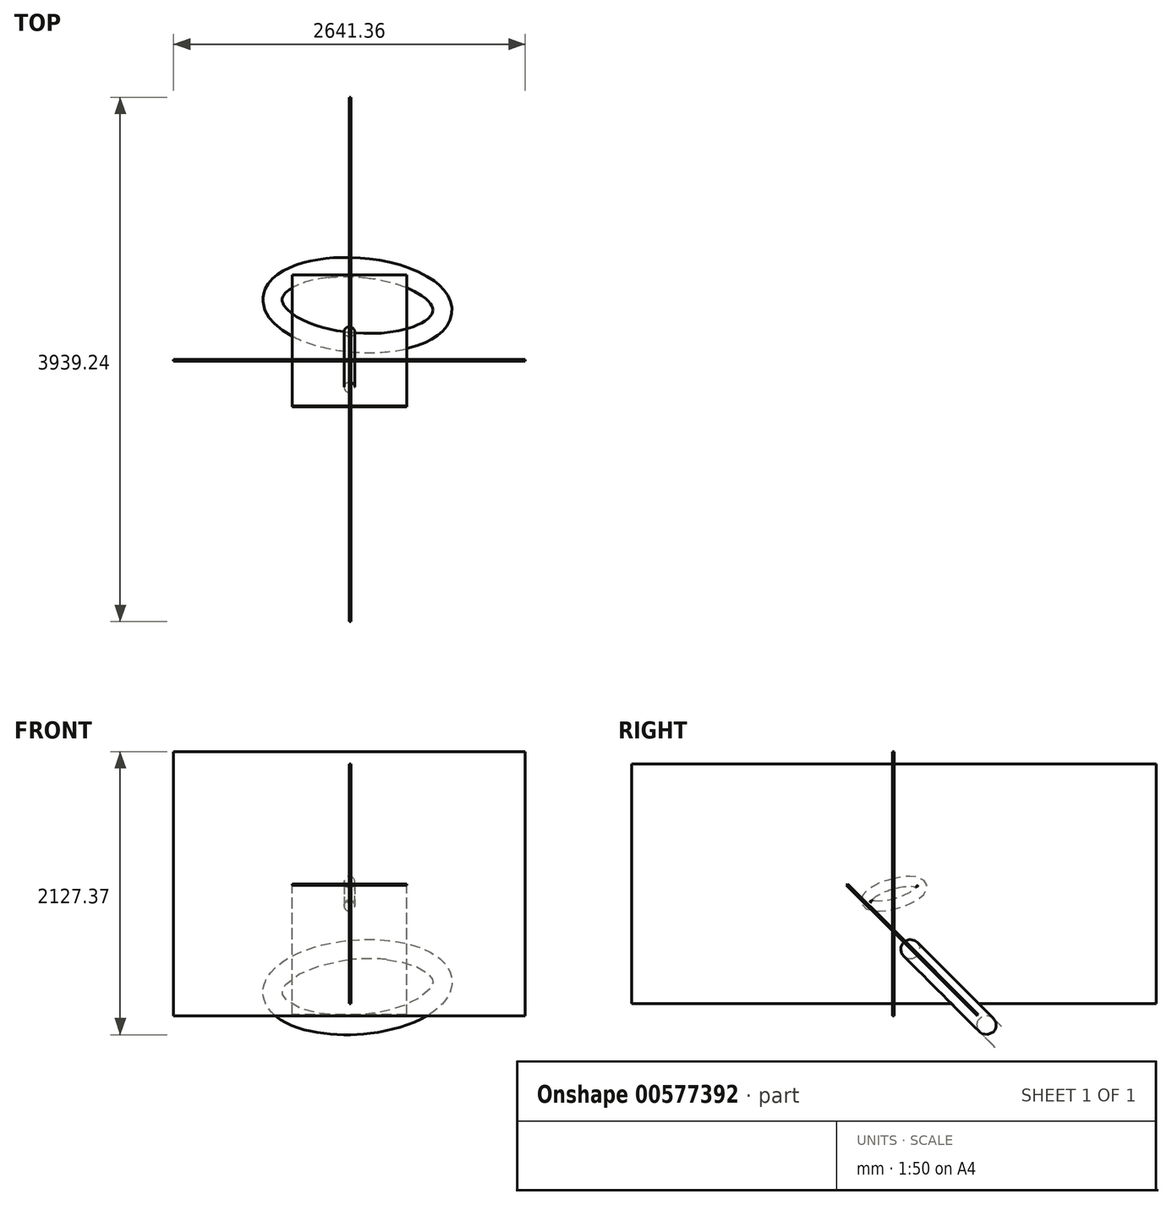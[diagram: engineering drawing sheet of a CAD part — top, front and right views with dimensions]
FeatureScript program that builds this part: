
annotation { "Feature Type Name" : "Feature", "Feature Type Description" : "" }
export const myFeature = defineFeature(function(context is Context, id is Id, definition is map)
    precondition{}
    {
        {
            var Q0;
            Q0=qCreatedBy(makeId("Front.planeOp"),FACE);
            var sketch = newSketch(context, id + "F0", { "sketchPlane" : qUnion([Q0])});
            skCircle(sketch, "E0", {"center": v(0, 0) * mm, "radius": 40.02 * mm});
            skSolve(sketch);
        }
        {
            var Q0;
            Q0=qCreatedBy(makeId("Right.planeOp"),FACE);
            var sketch = newSketch(context, id + "F1", { "sketchPlane" : qUnion([Q0])});
            skEllipse(sketch, "E1", {"center": v(0, -75.72) * mm, "majorRadius": 214.11 * mm, "minorRadius": 73.13 * mm, "majorAxis": v(0.96, 0.28)});
            skSolve(sketch);
        }
        {
            var Q0;
            Q0=makeQuery(id+"F0.imprint","IMPRINT",FACE,{"disambiguationData":[TD([[makeQuery(id+"F0.imprint","IMPRINT",EDGE,{"derivedFrom":sQuery(id+"F0.wireOp",EDGE,"E0")}),1.0]])]});
            var Q1;
            Q1=sQuery(id+"F1.wireOp",EDGE,"E1");
            sweep(context, id + "F2", {"profiles" : qUnion([Q0]), "path" : qUnion([Q1])});
        }
        {
            var Q0;
            Q0=qCreatedBy(makeId("Right.planeOp"),FACE);
            var sketch = newSketch(context, id + "F3", { "sketchPlane" : qUnion([Q0])});
            skPoint(sketch, "E2", {"position": v(131, -498.6) * mm});
            skCircle(sketch, "E3", {"center": v(131, -498.6) * mm, "radius": 72.46 * mm});
            skSolve(sketch);
        }
        {
            var Q0;
            Q0=qCreatedBy(makeId("Front.planeOp"),FACE);
            var sketch = newSketch(context, id + "F4", { "sketchPlane" : qUnion([Q0])});
            skPoint(sketch, "E4.0", {"position": v(0, -498.6) * mm});
            skEllipse(sketch, "E5", {"center": v(0, -498.6) * mm, "majorRadius": 547.9 * mm, "minorRadius": 370.15 * mm, "majorAxis": v(-0.65, -0.76)});
            skSolve(sketch);
        }
        {
            var Q0;
            Q0=makeQuery(id+"F4.imprint","IMPRINT",FACE,{"disambiguationData":[TD([[makeQuery(id+"F4.imprint","IMPRINT",EDGE,{"derivedFrom":sQuery(id+"F4.wireOp",EDGE,"E5")}),1.0]])]});
            var Q1;
            Q1=sQuery(id+"F3.wireOp",EDGE,"E3");
            cPlane(context, id + "F5", {"entities" : qUnion([Q0, Q1]), "cplaneType" : CPlaneType.LINE_ANGLE, "offset" : 25.4 * mm, "angle" : 45 * degree, "width" : 152.4 * mm, "height" : 152.4 * mm});
        }
        {
            var Q0;
            Q0=qCreatedBy(id+"F5.planeOp",FACE);
            var sketch = newSketch(context, id + "F6", { "sketchPlane" : qUnion([Q0])});
            skEllipse(sketch, "E6", {"center": v(-60.52, -838.67) * mm, "majorRadius": 398.08 * mm, "minorRadius": 641.65 * mm, "majorAxis": v(0.14, 1)});
            skSolve(sketch);
        }
        {
            var Q0;
            Q0=makeQuery(id+"F3.imprint","IMPRINT",FACE,{"disambiguationData":[TD([[makeQuery(id+"F3.imprint","IMPRINT",EDGE,{"derivedFrom":sQuery(id+"F3.wireOp",EDGE,"E3")}),1.0]])]});
            var Q1;
            Q1=sQuery(id+"F6.wireOp",EDGE,"E6");
            sweep(context, id + "F7", {"profiles" : qUnion([Q0]), "path" : qUnion([Q1])});
        }
        {
            var Q0;
            Q0=qCreatedBy(makeId("Front.planeOp"),FACE);
            var sketch = newSketch(context, id + "F8", { "sketchPlane" : qUnion([Q0])});
            skLineSegment(sketch, "E7.bottom", {"start": v(1320.68, -992.6) * mm, "end": v(-1320.68, -992.6) * mm});
            skLineSegment(sketch, "E7.top", {"start": v(1320.68, 992.6) * mm, "end": v(-1320.68, 992.6) * mm});
            skLineSegment(sketch, "E7.left", {"start": v(1320.68, -992.6) * mm, "end": v(1320.68, 992.6) * mm});
            skLineSegment(sketch, "E7.right", {"start": v(-1320.68, -992.6) * mm, "end": v(-1320.68, 992.6) * mm});
            skPoint(sketch, "E7.middle", {"position": v(0, 0) * mm});
            skSolve(sketch);
        }
        {
            var Q0;
            Q0 = qSketchRegion(id + "F8", true);
            extrude(context, id + "F9", {"entities" : qUnion([Q0]), "depth" : 12.7 * mm, "offsetDistance" : 25.4 * mm});
        }
        {
            var Q0;
            Q0=qCreatedBy(makeId("Right.planeOp"),FACE);
            var sketch = newSketch(context, id + "F10", { "sketchPlane" : qUnion([Q0])});
            skLineSegment(sketch, "E8.bottom", {"start": v(1969.62, -899.75) * mm, "end": v(-1969.62, -899.75) * mm});
            skLineSegment(sketch, "E8.top", {"start": v(1969.62, 899.75) * mm, "end": v(-1969.62, 899.75) * mm});
            skLineSegment(sketch, "E8.left", {"start": v(1969.62, -899.75) * mm, "end": v(1969.62, 899.75) * mm});
            skLineSegment(sketch, "E8.right", {"start": v(-1969.62, -899.75) * mm, "end": v(-1969.62, 899.75) * mm});
            skPoint(sketch, "E8.middle", {"position": v(0, 0) * mm});
            skSolve(sketch);
        }
        {
            var Q0;
            Q0 = qSketchRegion(id + "F10", true);
            extrude(context, id + "F11", {"entities" : qUnion([Q0]), "depth" : 12.7 * mm, "offsetDistance" : 25.4 * mm});
        }
        {
            var Q0;
            Q0=qCreatedBy(id+"F5.planeOp",FACE);
            var sketch = newSketch(context, id + "F12", { "sketchPlane" : qUnion([Q0])});
            skLineSegment(sketch, "E9.bottom", {"start": v(-430.66, -1143.95) * mm, "end": v(430.66, -1143.95) * mm});
            skLineSegment(sketch, "E9.top", {"start": v(-430.66, 244.11) * mm, "end": v(430.66, 244.11) * mm});
            skLineSegment(sketch, "E9.left", {"start": v(-430.66, -1143.95) * mm, "end": v(-430.66, 244.11) * mm});
            skLineSegment(sketch, "E9.right", {"start": v(430.66, -1143.95) * mm, "end": v(430.66, 244.11) * mm});
            skPoint(sketch, "E9.middle", {"position": v(0, -449.92) * mm});
            skSolve(sketch);
        }
        {
            var Q0;
            Q0 = qSketchRegion(id + "F12", true);
            extrude(context, id + "F13", {"entities" : qUnion([Q0]), "depth" : 12.7 * mm, "offsetDistance" : 25.4 * mm});
        }
    });
